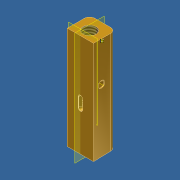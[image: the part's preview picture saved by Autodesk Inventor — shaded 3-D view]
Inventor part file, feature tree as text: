
AUTODESK INVENTOR PART (.ipt)
format: ipt  version: unknown  size: 333,312 bytes
history: native  units: in
note: dims shown in document units (in); Inventor stores cm internally (conversion verified against a paired STEP export)
features: sketch x13, extrude x6, hole x4, revolve x2, fillet x2, mirror x1, plane x1, other x1
ambient origin geometry x8: Origin, YZ Plane, XZ Plane, XY Plane, X Axis, Y Axis, Z Axis, Center Point
bodies: Solid1 (feature_tree)
feature tree (30):
  extrude  "Extrusion1"  Depth=0.156in
  extrude  "Extrusion2"  Depth=0.375in
  hole  "Hole1"  [1 undecoded]
  hole  "Hole4"  [1 undecoded]
  revolve  "Revolution1"  [1 undecoded]
  sketch  "Sketch12"  dims[d14=0.063in d15=0.5in d16=0.375in d17=0.25in d18=0.5635in d19=0.745in d20=0.0in]
  hole  "Hole5"  [1 undecoded]
  mirror  "Mirror1"
  extrude  "Extrusion4"  Depth=0.02in
  revolve  "Revolution2"  [1 undecoded]
  plane  "Work Plane7"
  hole  "Hole6"  [1 undecoded]
  fillet  "Fillet5"  Radius=0.1293in
  extrude  "Extrusion5"  Depth=0.0835in
  extrude  "Extrusion6"  Depth=0.025in
  extrude  "Extrusion9"  Depth=0.025in
  fillet  "Fillet6"  [1 undecoded]
  other  "Work Axis1"
  sketch  "Sketch1"  dims[d0=0.312in d1=0.156in]
  sketch  "Sketch2"  dims[d2=0.75in d3=0.375in]
  sketch  "Sketch3"  dims[d4=0.2656in d5=0.0in d6=0.05in]
  sketch  "Sketch10"  dims[d7=0.025in d8=0.11in]
  sketch  "Sketch11"  dims[d9=0.005in d10=0.0in d12=0.0in]
  sketch  "Sketch14"  dims[d65=0.156in d66=0.271in d67=0.375in d68=0.25in d69=0.5635in d70=0.25in d71=0.8108in d73=180.0deg]
  sketch  "Sketch16"  dims[d74=0.02in d75=0.02in]
  sketch  "Sketch17"  dims[d78=0.1875in d79=0.1875in]
  sketch  "Sketch18"  dims[d80=0.1875in d95=0.1562in]
  sketch  "Sketch19"  dims[d96=0.08in d97=0.5in d98=0.375in d99=0.25in d100=0.5635in d101=0.01in d102=0.8108in d104=0.1293in]
  sketch  "Sketch20"  dims[d105=0.0042in d106=0.0835in]
  sketch  "Sketch24"  dims[d107=0.0938in d108=0.0in d109=0.025in d110=0.025in d111=180.0deg d112=0.02in d113=0.02in d114=0.023in d115=0.023in d116=0.024in d117=0.012in d118=0.5in d119=0.375in d120=0.25in d121=0.5635in d122=0.0625in d123=0.8108in d125=0.003in d126=0.281in d127=0.0938in d128=0.1718in d129=0.3125in d130=0.125in d131=0.0in d132=1.0in d133=0.0in d139=0.3125in d140=0.312in d141=0.0in d142=0.0625in d143=0.4947in]
note: 7 required parameter values undecoded (feature->parameter linkage not recoverable at this tier; creation-order binding heuristic only, values carry confidence <= 0.55)